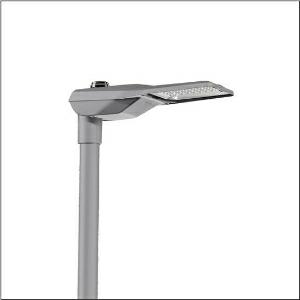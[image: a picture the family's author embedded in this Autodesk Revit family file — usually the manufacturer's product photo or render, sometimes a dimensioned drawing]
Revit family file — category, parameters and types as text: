
# Revit family: streetlight_sl_21_mini___st0_8a_5xe6c47n08jb_51ba
name_source: partatom
category: Lighting Fixtures
units: mm (PartAtom-declared; Revit-internal decimal feet)

## family parameters
Cut with Voids When Loaded = No
Host = Face
Light Source = No
Part Type = Normal
Room Calculation Point = No
Round Connector Dimension = Use Diameter
Shared = No

## types (1)
- --- (1 x LED, 13390 lm, 87.3 W, 4000K)
    Apparent Load = 87 VA
    CIE Flux Codes = 41 75 97 100 100
    Color Rendering = 70
    Color Temperature = 4000K
    Default Elevation = 1800 mm
    Description = Streetlight SL 21 mini, mast luminaire, primary light control with lens, of PMMA, primary optical cover: cover, of toughened safety glass, transparent, light distribution: ST0.8a, light emission: direct distribution, primary light characteristic: asymmetric, installation type: side-entry, LED, 3G 2.5mm², High Power LED, rated luminous flux: 13.390lm, luminous efficacy: 153lm/W, light colour: 740, colour temperature: 4000K, control gear: NEMA (7pin), control: overheat protection, pre-setting: linear dimming characteristic, constant luminous flux control, time-dependent luminous flux control, flexible luminous flux parameterisation, mains connection: 230..240V, AC, 50/60Hz, connection cable pre-assembled, cable length: 10,5m, wiring characteristics: H05VV-F, start of lifetime: 87W, end of service life: 90W, reduction: 40W, luminaire housing, of diecast aluminium (EN AC-44300), powder-coated, Siteco® metallic grey (DB 702S), corrosivity category C5 mid according to DIN EN ISO 12944, multi-level sealing system, sealing non-destructively replaceable, inclination adjustable: 0°, 5°, 10°, 15°, length: 628mm, width: 235mm, height: 110mm, spigot size: 42mm (side-entry), mounting height: 4..8m, protection rating (complete): IP66, insulation class (complete): insulation class I (protective earthing), certification: CE, ENEC, ENEC+, VDE, impact resistance: IK10, permissible operating ambient temperature for outdoor applications: -40..+50°C, standard-compliant lighting for roads and squares, packaging unit: 1 piece

Light Distribution: ST0.8a
    Height = 110 mm
    Lamp = 1 x LED
    Lamp Light Flux = 13390 lm
    Lamp Power = 87.3 W
    Lamp count = 1
    Length = 625 mm
    Luminous efficacy = 153 lm/W
    Manufacturer = Siteco
    ModVariant = No
    Model = 5XE6C47N08JB
    Number of Poles = 1
    OnlyDefault = Yes
    Power Factor = 1
    Product Name = Streetlight SL 21 mini | ST0.8a
    Product group = mast luminaire | pylon top
    ProductGroupID = 6100
    Protection Class = Protection class I
    Protection Degree = IP 66
    RLX_Detail_Level = 1
    RLX_Emergency_Light_Flux = 0 lm
    RLX_Emergency_Type = 0
    RLX_Emergency_Type_DB = No
    RlxData = <blob elided: 26089 chars, md5=793fa9cb>
    Socket = socket
    Standby Power = 0 W
    System Light Flux = 13390 lm
    System Power = 87 W
    Type Comments = factory setting: luminous flux: 100 % | dim-lin: 254 | 915 mA
    Type Image = l_1294379.jpg
    URL = http://relux.com
    VarID = @adj_155391
    Voltage = 0 V
    Weight = 0.00 kg
    Width = 234 mm

## geometry (parser evidence)
native form markers: Blend x4, Sweep x11
no freeform markers — native parametric forms only
